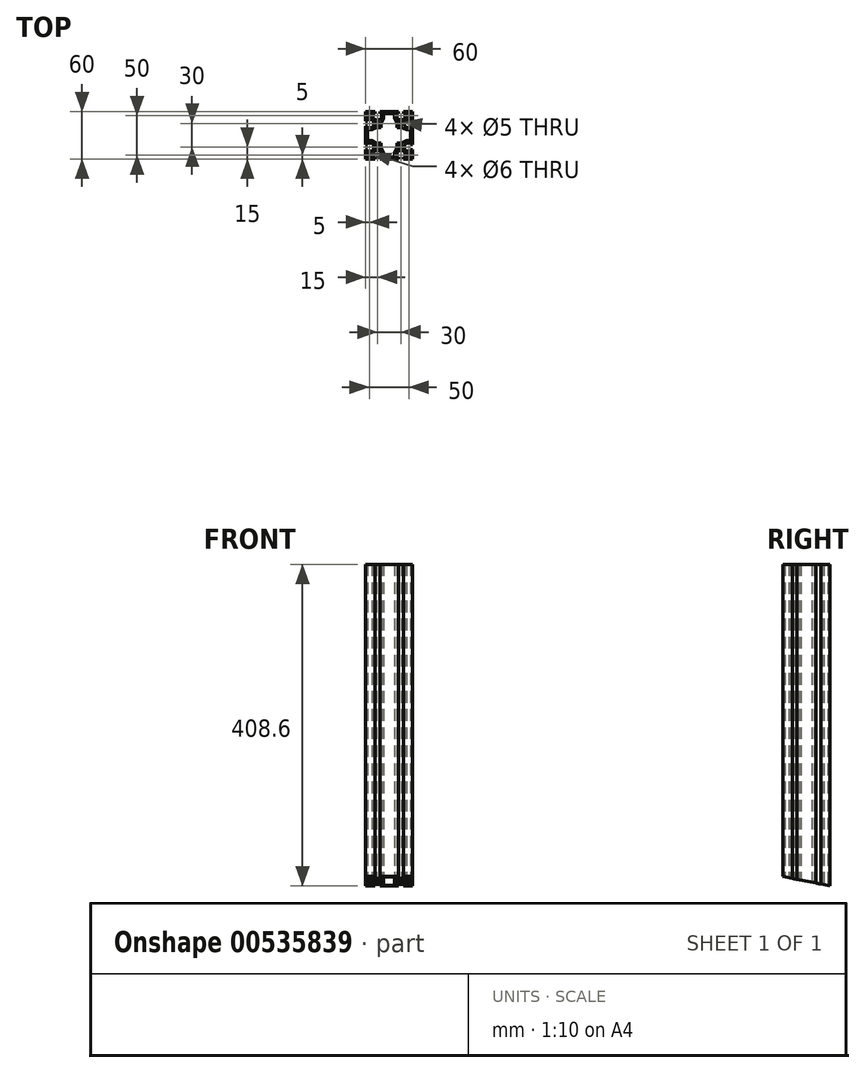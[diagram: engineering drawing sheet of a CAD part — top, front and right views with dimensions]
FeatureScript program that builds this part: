
annotation { "Feature Type Name" : "Feature", "Feature Type Description" : "" }
export const myFeature = defineFeature(function(context is Context, id is Id, definition is map)
    precondition{}
    {
        {
            var Q0;
            Q0=qCreatedBy(makeId("Top.planeOp"),FACE);
            var sketch = newSketch(context, id + "F0", { "sketchPlane" : qUnion([Q0])});
            skLineSegment(sketch, "E0.bottom", {"start": v(30, -30) * mm, "end": v(-30, -30) * mm});
            skLineSegment(sketch, "E0.top", {"start": v(30, 30) * mm, "end": v(-30, 30) * mm});
            skLineSegment(sketch, "E0.left", {"start": v(30, -30) * mm, "end": v(30, 30) * mm});
            skLineSegment(sketch, "E0.right", {"start": v(-30, -30) * mm, "end": v(-30, 30) * mm});
            skPoint(sketch, "E0.middle", {"position": v(0, 0) * mm});
            skLineSegment(sketch, "E1.top", {"start": v(-11.85, 30) * mm, "end": v(-18.15, 30) * mm});
            skLineSegment(sketch, "E1.left", {"start": v(-11.85, 27.5) * mm, "end": v(-11.85, 30) * mm});
            skLineSegment(sketch, "E1.right", {"start": v(-18.15, 27.5) * mm, "end": v(-18.15, 30) * mm});
            skPoint(sketch, "E1.middle", {"position": v(-15, 28.75) * mm});
            skLineSegment(sketch, "E2.bottom", {"start": v(-9.85, 27.5) * mm, "end": v(-11.85, 27.5) * mm});
            skLineSegment(sketch, "E2.left", {"start": v(-9.85, 27.5) * mm, "end": v(-9.85, 21.55) * mm});
            skLineSegment(sketch, "E2.right", {"start": v(-20.15, 27.5) * mm, "end": v(-20.15, 21.55) * mm});
            skPoint(sketch, "E2.middle", {"position": v(-15, 24.52) * mm});
            skArc(sketch, "E3", {"start": v(-20.15, 21.55) * mm, "mid": v(-15, 19.5) * mm, "end": v(-9.85, 21.55) * mm});
            skPoint(sketch, "E4.MirrorP", {"position": v(15, 24.52) * mm});
            skPoint(sketch, "E5.MirrorP", {"position": v(15, 28.75) * mm});
            skLineSegment(sketch, "E6.MirrorCS", {"start": v(11.85, 27.5) * mm, "end": v(11.85, 30) * mm});
            skLineSegment(sketch, "E7.MirrorCS", {"start": v(18.15, 27.5) * mm, "end": v(18.15, 30) * mm});
            skLineSegment(sketch, "E8.MirrorCS", {"start": v(9.85, 27.5) * mm, "end": v(11.85, 27.5) * mm});
            skLineSegment(sketch, "E9.MirrorCS", {"start": v(9.85, 27.5) * mm, "end": v(9.85, 21.55) * mm});
            skArc(sketch, "E10.MirrorCS", {"start": v(20.15, 21.55) * mm, "mid": v(15, 19.5) * mm, "end": v(9.85, 21.55) * mm});
            skLineSegment(sketch, "E11.MirrorCS", {"start": v(20.15, 27.5) * mm, "end": v(20.15, 21.55) * mm});
            skLineSegment(sketch, "E12.MirrorCS", {"start": v(11.85, 30) * mm, "end": v(18.15, 30) * mm});
            skLineSegment(sketch, "E13.1.0", {"start": v(27.5, 20.15) * mm, "end": v(21.55, 20.15) * mm});
            skLineSegment(sketch, "E13.1.1", {"start": v(27.5, 9.85) * mm, "end": v(21.55, 9.85) * mm});
            skArc(sketch, "E13.1.2", {"start": v(21.55, 20.15) * mm, "mid": v(19.5, 15) * mm, "end": v(21.55, 9.85) * mm});
            skLineSegment(sketch, "E13.1.3", {"start": v(27.5, -9.85) * mm, "end": v(21.55, -9.85) * mm});
            skLineSegment(sketch, "E13.1.4", {"start": v(27.5, -20.15) * mm, "end": v(21.55, -20.15) * mm});
            skPoint(sketch, "E13.1.5", {"position": v(28.75, 15) * mm});
            skPoint(sketch, "E13.1.6", {"position": v(28.75, -15) * mm});
            skArc(sketch, "E13.1.7", {"start": v(21.55, -20.15) * mm, "mid": v(19.5, -15) * mm, "end": v(21.55, -9.85) * mm});
            skPoint(sketch, "E13.1.8", {"position": v(24.52, -15) * mm});
            skPoint(sketch, "E13.1.9", {"position": v(24.52, 15) * mm});
            skLineSegment(sketch, "E13.1.10", {"start": v(27.5, 9.85) * mm, "end": v(27.5, 20.15) * mm});
            skLineSegment(sketch, "E13.1.11", {"start": v(27.5, -11.85) * mm, "end": v(27.5, -18.15) * mm});
            skLineSegment(sketch, "E13.1.12", {"start": v(30, 11.85) * mm, "end": v(30, 18.15) * mm});
            skLineSegment(sketch, "E13.1.13", {"start": v(30, -11.85) * mm, "end": v(30, -18.15) * mm});
            skLineSegment(sketch, "E13.1.14", {"start": v(27.5, 18.15) * mm, "end": v(30, 18.15) * mm});
            skLineSegment(sketch, "E13.1.15", {"start": v(27.5, 11.85) * mm, "end": v(30, 11.85) * mm});
            skLineSegment(sketch, "E13.1.16", {"start": v(27.5, 11.85) * mm, "end": v(27.5, 18.15) * mm});
            skLineSegment(sketch, "E13.1.17", {"start": v(27.5, -9.85) * mm, "end": v(27.5, -20.15) * mm});
            skLineSegment(sketch, "E13.1.18", {"start": v(27.5, -18.15) * mm, "end": v(30, -18.15) * mm});
            skLineSegment(sketch, "E13.1.19", {"start": v(27.5, -11.85) * mm, "end": v(30, -11.85) * mm});
            skLineSegment(sketch, "E13.2.0", {"start": v(20.15, -27.5) * mm, "end": v(20.15, -21.55) * mm});
            skLineSegment(sketch, "E13.2.1", {"start": v(9.85, -27.5) * mm, "end": v(9.85, -21.55) * mm});
            skArc(sketch, "E13.2.2", {"start": v(20.15, -21.55) * mm, "mid": v(15, -19.5) * mm, "end": v(9.85, -21.55) * mm});
            skLineSegment(sketch, "E13.2.3", {"start": v(-9.85, -27.5) * mm, "end": v(-9.85, -21.55) * mm});
            skLineSegment(sketch, "E13.2.4", {"start": v(-20.15, -27.5) * mm, "end": v(-20.15, -21.55) * mm});
            skPoint(sketch, "E13.2.5", {"position": v(15, -28.75) * mm});
            skPoint(sketch, "E13.2.6", {"position": v(-15, -28.75) * mm});
            skArc(sketch, "E13.2.7", {"start": v(-20.15, -21.55) * mm, "mid": v(-15, -19.5) * mm, "end": v(-9.85, -21.55) * mm});
            skPoint(sketch, "E13.2.8", {"position": v(-15, -24.52) * mm});
            skPoint(sketch, "E13.2.9", {"position": v(15, -24.52) * mm});
            skLineSegment(sketch, "E13.2.10", {"start": v(9.85, -27.5) * mm, "end": v(20.15, -27.5) * mm});
            skLineSegment(sketch, "E13.2.11", {"start": v(-11.85, -27.5) * mm, "end": v(-18.15, -27.5) * mm});
            skLineSegment(sketch, "E13.2.12", {"start": v(11.85, -30) * mm, "end": v(18.15, -30) * mm});
            skLineSegment(sketch, "E13.2.13", {"start": v(-11.85, -30) * mm, "end": v(-18.15, -30) * mm});
            skLineSegment(sketch, "E13.2.14", {"start": v(18.15, -27.5) * mm, "end": v(18.15, -30) * mm});
            skLineSegment(sketch, "E13.2.15", {"start": v(11.85, -27.5) * mm, "end": v(11.85, -30) * mm});
            skLineSegment(sketch, "E13.2.16", {"start": v(11.85, -27.5) * mm, "end": v(18.15, -27.5) * mm});
            skLineSegment(sketch, "E13.2.17", {"start": v(-9.85, -27.5) * mm, "end": v(-20.15, -27.5) * mm});
            skLineSegment(sketch, "E13.2.18", {"start": v(-18.15, -27.5) * mm, "end": v(-18.15, -30) * mm});
            skLineSegment(sketch, "E13.2.19", {"start": v(-11.85, -27.5) * mm, "end": v(-11.85, -30) * mm});
            skLineSegment(sketch, "E13.3.0", {"start": v(-27.5, -20.15) * mm, "end": v(-21.55, -20.15) * mm});
            skLineSegment(sketch, "E13.3.1", {"start": v(-27.5, -9.85) * mm, "end": v(-21.55, -9.85) * mm});
            skArc(sketch, "E13.3.2", {"start": v(-21.55, -20.15) * mm, "mid": v(-19.5, -15) * mm, "end": v(-21.55, -9.85) * mm});
            skLineSegment(sketch, "E13.3.3", {"start": v(-27.5, 9.85) * mm, "end": v(-21.55, 9.85) * mm});
            skLineSegment(sketch, "E13.3.4", {"start": v(-27.5, 20.15) * mm, "end": v(-21.55, 20.15) * mm});
            skPoint(sketch, "E13.3.5", {"position": v(-28.75, -15) * mm});
            skPoint(sketch, "E13.3.6", {"position": v(-28.75, 15) * mm});
            skArc(sketch, "E13.3.7", {"start": v(-21.55, 20.15) * mm, "mid": v(-19.5, 15) * mm, "end": v(-21.55, 9.85) * mm});
            skPoint(sketch, "E13.3.8", {"position": v(-24.52, 15) * mm});
            skPoint(sketch, "E13.3.9", {"position": v(-24.52, -15) * mm});
            skLineSegment(sketch, "E13.3.10", {"start": v(-27.5, -9.85) * mm, "end": v(-27.5, -20.15) * mm});
            skLineSegment(sketch, "E13.3.11", {"start": v(-27.5, 11.85) * mm, "end": v(-27.5, 18.15) * mm});
            skLineSegment(sketch, "E13.3.12", {"start": v(-30, -11.85) * mm, "end": v(-30, -18.15) * mm});
            skLineSegment(sketch, "E13.3.13", {"start": v(-30, 11.85) * mm, "end": v(-30, 18.15) * mm});
            skLineSegment(sketch, "E13.3.14", {"start": v(-27.5, -18.15) * mm, "end": v(-30, -18.15) * mm});
            skLineSegment(sketch, "E13.3.15", {"start": v(-27.5, -11.85) * mm, "end": v(-30, -11.85) * mm});
            skLineSegment(sketch, "E13.3.16", {"start": v(-27.5, -11.85) * mm, "end": v(-27.5, -18.15) * mm});
            skLineSegment(sketch, "E13.3.17", {"start": v(-27.5, 9.85) * mm, "end": v(-27.5, 20.15) * mm});
            skLineSegment(sketch, "E13.3.18", {"start": v(-27.5, 18.15) * mm, "end": v(-30, 18.15) * mm});
            skLineSegment(sketch, "E13.3.19", {"start": v(-27.5, 11.85) * mm, "end": v(-30, 11.85) * mm});
            skLineSegment(sketch, "E13.anchor1", {"start": v(0, 0) * mm, "end": v(-20.15, 21.55) * mm, "construction": true});
            skLineSegment(sketch, "E13.anchor2", {"start": v(0, 0) * mm, "end": v(-21.55, -20.15) * mm, "construction": true});
            skLineSegment(sketch, "E14.trimOffspring", {"start": v(-18.15, 27.5) * mm, "end": v(-20.15, 27.5) * mm});
            skLineSegment(sketch, "E15.trimOffspring", {"start": v(18.15, 27.5) * mm, "end": v(20.15, 27.5) * mm});
            skCircle(sketch, "E16", {"center": v(-15, 15) * mm, "radius": 2.5 * mm});
            skCircle(sketch, "E17", {"center": v(-25, 25) * mm, "radius": 3 * mm});
            skCircle(sketch, "E18.MirrorC", {"center": v(25, 25) * mm, "radius": 3 * mm});
            skCircle(sketch, "E19.MirrorC", {"center": v(25, -25) * mm, "radius": 3 * mm});
            skCircle(sketch, "E20.MirrorC", {"center": v(-25, -25) * mm, "radius": 3 * mm});
            skCircle(sketch, "E21.MirrorC", {"center": v(15, 15) * mm, "radius": 2.5 * mm});
            skCircle(sketch, "E22.MirrorC", {"center": v(15, -15) * mm, "radius": 2.5 * mm});
            skCircle(sketch, "E23.MirrorC", {"center": v(-15, -15) * mm, "radius": 2.5 * mm});
            skLineSegment(sketch, "E24", {"start": v(-7, 27.5) * mm, "end": v(0, 27.5) * mm});
            skLineSegment(sketch, "E25", {"start": v(-7, 27.5) * mm, "end": v(-7, 22) * mm});
            skLineSegment(sketch, "E26", {"start": v(-10, 10) * mm, "end": v(-10, 16) * mm});
            skLineSegment(sketch, "E27", {"start": v(-10, 16) * mm, "end": v(-7, 22) * mm});
            skLineSegment(sketch, "E28.MirrorCS", {"start": v(10, 10) * mm, "end": v(10, 16) * mm});
            skLineSegment(sketch, "E29.MirrorCS", {"start": v(10, 16) * mm, "end": v(7, 22) * mm});
            skLineSegment(sketch, "E30.MirrorCS", {"start": v(7, 27.5) * mm, "end": v(0, 27.5) * mm});
            skLineSegment(sketch, "E31.MirrorCS", {"start": v(7, 27.5) * mm, "end": v(7, 22) * mm});
            skLineSegment(sketch, "E32.1.0", {"start": v(-10, -10) * mm, "end": v(-16, -10) * mm});
            skLineSegment(sketch, "E32.1.1", {"start": v(-16, -10) * mm, "end": v(-22, -7) * mm});
            skLineSegment(sketch, "E32.1.2", {"start": v(-27.5, -7) * mm, "end": v(-22, -7) * mm});
            skLineSegment(sketch, "E32.1.3", {"start": v(-27.5, -7) * mm, "end": v(-27.5, 0) * mm});
            skLineSegment(sketch, "E32.1.4", {"start": v(-27.5, 7) * mm, "end": v(-27.5, 0) * mm});
            skLineSegment(sketch, "E32.1.5", {"start": v(-27.5, 7) * mm, "end": v(-22, 7) * mm});
            skLineSegment(sketch, "E32.1.6", {"start": v(-16, 10) * mm, "end": v(-22, 7) * mm});
            skLineSegment(sketch, "E32.1.7", {"start": v(-10, 10) * mm, "end": v(-16, 10) * mm});
            skLineSegment(sketch, "E32.2.0", {"start": v(10, -10) * mm, "end": v(10, -16) * mm});
            skLineSegment(sketch, "E32.2.1", {"start": v(10, -16) * mm, "end": v(7, -22) * mm});
            skLineSegment(sketch, "E32.2.2", {"start": v(7, -27.5) * mm, "end": v(7, -22) * mm});
            skLineSegment(sketch, "E32.2.3", {"start": v(7, -27.5) * mm, "end": v(0, -27.5) * mm});
            skLineSegment(sketch, "E32.2.4", {"start": v(-7, -27.5) * mm, "end": v(0, -27.5) * mm});
            skLineSegment(sketch, "E32.2.5", {"start": v(-7, -27.5) * mm, "end": v(-7, -22) * mm});
            skLineSegment(sketch, "E32.2.6", {"start": v(-10, -16) * mm, "end": v(-7, -22) * mm});
            skLineSegment(sketch, "E32.2.7", {"start": v(-10, -10) * mm, "end": v(-10, -16) * mm});
            skLineSegment(sketch, "E32.3.0", {"start": v(10, 10) * mm, "end": v(16, 10) * mm});
            skLineSegment(sketch, "E32.3.1", {"start": v(16, 10) * mm, "end": v(22, 7) * mm});
            skLineSegment(sketch, "E32.3.2", {"start": v(27.5, 7) * mm, "end": v(22, 7) * mm});
            skLineSegment(sketch, "E32.3.3", {"start": v(27.5, 7) * mm, "end": v(27.5, 0) * mm});
            skLineSegment(sketch, "E32.3.4", {"start": v(27.5, -7) * mm, "end": v(27.5, 0) * mm});
            skLineSegment(sketch, "E32.3.5", {"start": v(27.5, -7) * mm, "end": v(22, -7) * mm});
            skLineSegment(sketch, "E32.3.6", {"start": v(16, -10) * mm, "end": v(22, -7) * mm});
            skLineSegment(sketch, "E32.3.7", {"start": v(10, -10) * mm, "end": v(16, -10) * mm});
            skSolve(sketch);
        }
        {
            var Q0;
            {var subQ30=sQuery(id+"F0.wireOp",EDGE,"E1.left");Q0=makeQuery(id+"F0.imprint","IMPRINT",FACE,{"disambiguationData":[TD([[makeQuery(id+"F0.imprint","IMPRINT",EDGE,{"derivedFrom":subQ30}),-1.0]])]});}
            extrude(context, id + "F1", {"entities" : qUnion([Q0]), "depth" : 408.6 * mm, "offsetDistance" : 25 * mm});
        }
        {
            var Q0;
            Q0=makeQuery(id+"F1.opExtrude","SWEPT_EDGE",EDGE,{"disambiguationData":[OSD([sQuery(id+"F0.wireOp",EDGE,"E24"),sQuery(id+"F0.wireOp",EDGE,"E25")])]});
            var Q1;
            Q1=makeQuery(id+"F1.opExtrude","SWEPT_EDGE",EDGE,{"disambiguationData":[OSD([sQuery(id+"F0.wireOp",EDGE,"E30.MirrorCS"),sQuery(id+"F0.wireOp",EDGE,"E31.MirrorCS")])]});
            var Q2;
            Q2=makeQuery(id+"F1.opExtrude","SWEPT_EDGE",EDGE,{"disambiguationData":[OSD([sQuery(id+"F0.wireOp",EDGE,"840db5bc-c403-45cd-90c7-254e62d9e8c5.3.2"),sQuery(id+"F0.wireOp",EDGE,"840db5bc-c403-45cd-90c7-254e62d9e8c5.3.3")])]});
            var Q3;
            Q3=makeQuery(id+"F1.opExtrude","SWEPT_EDGE",EDGE,{"disambiguationData":[OSD([sQuery(id+"F0.wireOp",EDGE,"840db5bc-c403-45cd-90c7-254e62d9e8c5.3.4"),sQuery(id+"F0.wireOp",EDGE,"840db5bc-c403-45cd-90c7-254e62d9e8c5.3.5")])]});
            var Q4;
            Q4=makeQuery(id+"F1.opExtrude","SWEPT_EDGE",EDGE,{"disambiguationData":[OSD([sQuery(id+"F0.wireOp",EDGE,"840db5bc-c403-45cd-90c7-254e62d9e8c5.1.4"),sQuery(id+"F0.wireOp",EDGE,"840db5bc-c403-45cd-90c7-254e62d9e8c5.1.5")])]});
            var Q5;
            Q5=makeQuery(id+"F1.opExtrude","SWEPT_EDGE",EDGE,{"disambiguationData":[OSD([sQuery(id+"F0.wireOp",EDGE,"840db5bc-c403-45cd-90c7-254e62d9e8c5.1.2"),sQuery(id+"F0.wireOp",EDGE,"840db5bc-c403-45cd-90c7-254e62d9e8c5.1.3")])]});
            var Q6;
            Q6=makeQuery(id+"F1.opExtrude","SWEPT_EDGE",EDGE,{"disambiguationData":[OSD([sQuery(id+"F0.wireOp",EDGE,"840db5bc-c403-45cd-90c7-254e62d9e8c5.2.2"),sQuery(id+"F0.wireOp",EDGE,"840db5bc-c403-45cd-90c7-254e62d9e8c5.2.3")])]});
            var Q7;
            Q7=makeQuery(id+"F1.opExtrude","SWEPT_EDGE",EDGE,{"disambiguationData":[OSD([sQuery(id+"F0.wireOp",EDGE,"840db5bc-c403-45cd-90c7-254e62d9e8c5.2.4"),sQuery(id+"F0.wireOp",EDGE,"840db5bc-c403-45cd-90c7-254e62d9e8c5.2.5")])]});
            fillet(context, id + "F2", {"entities" : qUnion([Q0, Q1, Q2, Q3, Q4, Q5, Q6, Q7]), "radius" : 2 * mm, "tangentPropagation" : true, "allowEdgeOverflow" : false});
        }
        {
            var Q0;
            Q0=makeQuery(id+"F1.opExtrude","SWEPT_EDGE",EDGE,{"disambiguationData":[OSD([sQuery(id+"F0.wireOp",EDGE,"E26"),sQuery(id+"F0.wireOp",EDGE,"E27")])]});
            var Q1;
            Q1=makeQuery(id+"F1.opExtrude","SWEPT_EDGE",EDGE,{"disambiguationData":[OSD([sQuery(id+"F0.wireOp",EDGE,"E28.MirrorCS"),sQuery(id+"F0.wireOp",EDGE,"E29.MirrorCS")])]});
            var Q2;
            Q2=makeQuery(id+"F1.opExtrude","SWEPT_EDGE",EDGE,{"disambiguationData":[OSD([sQuery(id+"F0.wireOp",EDGE,"840db5bc-c403-45cd-90c7-254e62d9e8c5.3.0"),sQuery(id+"F0.wireOp",EDGE,"840db5bc-c403-45cd-90c7-254e62d9e8c5.3.1")])]});
            var Q3;
            Q3=makeQuery(id+"F1.opExtrude","SWEPT_EDGE",EDGE,{"disambiguationData":[OSD([sQuery(id+"F0.wireOp",EDGE,"840db5bc-c403-45cd-90c7-254e62d9e8c5.1.6"),sQuery(id+"F0.wireOp",EDGE,"840db5bc-c403-45cd-90c7-254e62d9e8c5.1.7")])]});
            var Q4;
            Q4=makeQuery(id+"F1.opExtrude","SWEPT_EDGE",EDGE,{"disambiguationData":[OSD([sQuery(id+"F0.wireOp",EDGE,"840db5bc-c403-45cd-90c7-254e62d9e8c5.1.0"),sQuery(id+"F0.wireOp",EDGE,"840db5bc-c403-45cd-90c7-254e62d9e8c5.1.1")])]});
            var Q5;
            Q5=makeQuery(id+"F1.opExtrude","SWEPT_EDGE",EDGE,{"disambiguationData":[OSD([sQuery(id+"F0.wireOp",EDGE,"840db5bc-c403-45cd-90c7-254e62d9e8c5.3.6"),sQuery(id+"F0.wireOp",EDGE,"840db5bc-c403-45cd-90c7-254e62d9e8c5.3.7")])]});
            var Q6;
            Q6=makeQuery(id+"F1.opExtrude","SWEPT_EDGE",EDGE,{"disambiguationData":[OSD([sQuery(id+"F0.wireOp",EDGE,"840db5bc-c403-45cd-90c7-254e62d9e8c5.2.0"),sQuery(id+"F0.wireOp",EDGE,"840db5bc-c403-45cd-90c7-254e62d9e8c5.2.1")])]});
            var Q7;
            Q7=makeQuery(id+"F1.opExtrude","SWEPT_EDGE",EDGE,{"disambiguationData":[OSD([sQuery(id+"F0.wireOp",EDGE,"840db5bc-c403-45cd-90c7-254e62d9e8c5.2.6"),sQuery(id+"F0.wireOp",EDGE,"840db5bc-c403-45cd-90c7-254e62d9e8c5.2.7")])]});
            fillet(context, id + "F3", {"entities" : qUnion([Q0, Q1, Q2, Q3, Q4, Q5, Q6, Q7]), "radius" : 7 * mm, "tangentPropagation" : true, "allowEdgeOverflow" : false});
        }
        {
            var Q0;
            Q0=qCreatedBy(makeId("Right.planeOp"),FACE);
            var sketch = newSketch(context, id + "F4", { "sketchPlane" : qUnion([Q0])});
            skLineSegment(sketch, "E33.MirrorCS", {"start": v(-188.6, -83.55) * mm, "end": v(5.7, -122.2) * mm});
            skLineSegment(sketch, "E34.MirrorCS", {"start": v(-164.29, 38.65) * mm, "end": v(30, 0) * mm});
            skLineSegment(sketch, "E35.MirrorCS", {"start": v(-164.29, 38.65) * mm, "end": v(-188.6, -83.55) * mm});
            skLineSegment(sketch, "E36.MirrorCS", {"start": v(30, 0) * mm, "end": v(5.7, -122.2) * mm});
            skSolve(sketch);
        }
        {
            var Q0;
            Q0=qSketchRegion(id+"F4",true);
            extrude(context, id + "F5", {"entities" : qUnion([Q0]), "operationType" : NewBodyOperationType.REMOVE, "depth" : 30 * mm, "offsetDistance" : 25 * mm, "hasSecondDirection" : true, "secondDirectionOppositeDirection" : true, "secondDirectionDepth" : 30 * mm});
        }
    });
